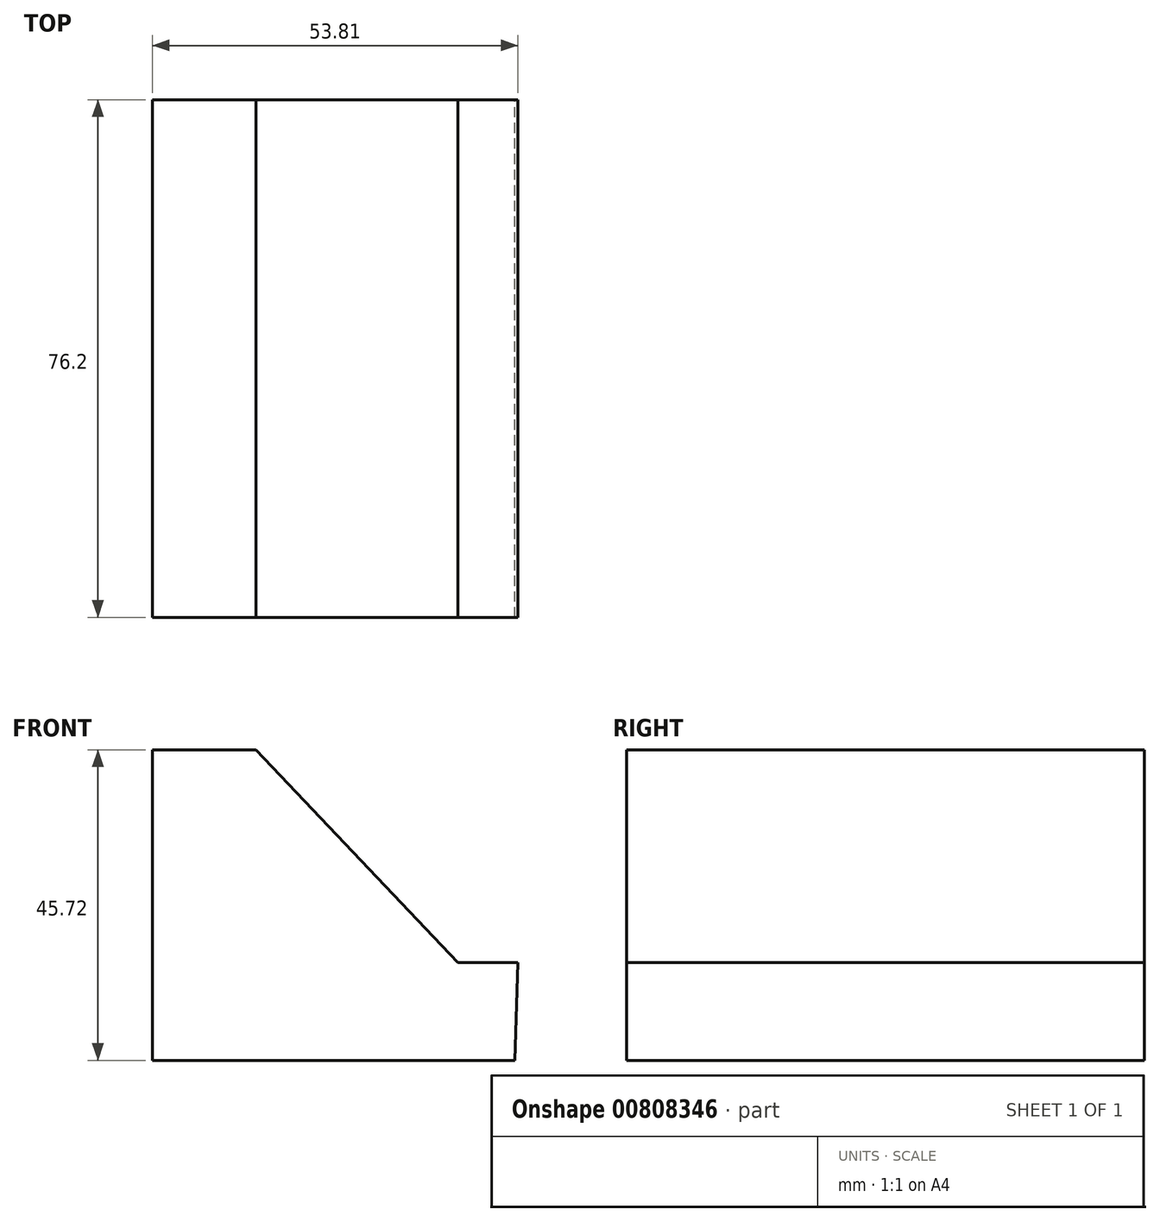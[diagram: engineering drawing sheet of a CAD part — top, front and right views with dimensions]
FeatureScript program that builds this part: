
annotation { "Feature Type Name" : "Feature", "Feature Type Description" : "" }
export const myFeature = defineFeature(function(context is Context, id is Id, definition is map)
    precondition{}
    {
        {
            var Q0;
            Q0=qCreatedBy(makeId("Front.planeOp"),FACE);
            var sketch = newSketch(context, id + "F0", { "sketchPlane" : qUnion([Q0])});
            skLineSegment(sketch, "E0", {"start": v(0, 0) * mm, "end": v(53.34, 0) * mm});
            skLineSegment(sketch, "E1", {"start": v(53.34, 0) * mm, "end": v(53.34, 0) * mm});
            skLineSegment(sketch, "E2", {"start": v(0, 0) * mm, "end": v(0, 45.72) * mm});
            skLineSegment(sketch, "E3", {"start": v(0, 45.72) * mm, "end": v(15.24, 45.72) * mm});
            skLineSegment(sketch, "E4", {"start": v(15.24, 45.72) * mm, "end": v(44.99, 14.42) * mm});
            skLineSegment(sketch, "E5", {"start": v(44.99, 14.42) * mm, "end": v(53.8, 14.42) * mm});
            skLineSegment(sketch, "E6", {"start": v(53.8, 14.42) * mm, "end": v(53.34, 0) * mm});
            skLineSegment(sketch, "E7", {"start": v(111.49, 8.22) * mm, "end": v(127.61, 8.22) * mm});
            skLineSegment(sketch, "E8", {"start": v(127.61, 8.22) * mm, "end": v(111.49, 8.22) * mm});
            skSolve(sketch);
        }
        {
            var Q0;
            Q0 = qSketchRegion(id + "F0", true);
            extrude(context, id + "F1", {"entities" : qUnion([Q0]), "depth" : 76.2 * mm, "offsetDistance" : 25.4 * mm});
        }
    });
